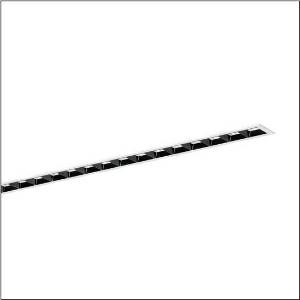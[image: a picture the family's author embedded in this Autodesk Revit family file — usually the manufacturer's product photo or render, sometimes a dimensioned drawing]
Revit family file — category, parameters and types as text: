
# Revit family: silica_r__21_51mx12dc4awb_60db
name_source: partatom
category: Lighting Fixtures
units: mm (PartAtom-declared; Revit-internal decimal feet)

## family parameters
Cut with Voids When Loaded = No
Host = Face
Light Source = No
Part Type = Normal
Room Calculation Point = No
Round Connector Dimension = Use Diameter
Shared = No

## types (1)
- --- (1 x LED, 10800 lm, 64.7 W, 4000K)
    Apparent Load = 65 VA
    CIE Flux Codes = 86 100 100 100 100
    Color Rendering = 80
    Color Temperature = 4000K
    Default Elevation = 1800 mm
    Description = Silica® 21, office luminaire, primary light control with darklight reflector, of PMMA, black, CAT 2 (L<= 3000cd/m²), light emission: direct distribution, primary light characteristic: symmetric, installation type: recessed, LED, rated luminous flux: 10.800lm, luminous efficacy: 167lm/W, light colour: 840, colour temperature: 4000K, with terminal, 3+2-pole, max. 2.5mm², mains connection: 220..240V, AC, 50/60Hz, rated input power: 64.7W, luminaire housing, of aluminium, traffic white (RAL 9016), length: 3.028mm, width: 79mm, height: 53mm, protection rating (complete): IP20, insulation class (complete): insulation class I (protective earthing), certification: CE, permissible operating ambient temperature: 0..+35°C, standard: EN 50419, packaging unit: 1 piece
    Height = 0 mm  [stored 0 ft]
    Lamp = 1 x LED
    Lamp Light Flux = 10800 lm
    Lamp Power = 64.7 W
    Lamp count = 1
    Length = 3027 mm
    Luminous efficacy = 167 lm/W
    Manufacturer = Siteco
    ModVariant = No
    Model = 51MX12DC4AWB
    Mounting Place = Ceiling
    Mounting Type = Recessed
    Number of Poles = 1
    OnlyDefault = Yes
    Power Factor = 1
    Product Name = Silica® 21
    Product group = office luminaire | ceiling recessed
    ProductGroupID = 400
    Protection Class = Protection class I
    Protection Degree = IP 20
    RLX_Detail_Level = 1
    RlxData = <blob elided: 62773 chars, md5=38e0fbbe>
    Socket = socket
    Standby Power = 0 W
    System Light Flux = 10800 lm
    System Power = 65 W
    Type Comments = factory setting: luminous flux: 100 % | dim-lin: 254 | 366 mA
    Type Image = l_1251632.jpg
    URL = http://relux.com
    VarID = @adj_034067
    Voltage = 0 V
    Weight = 0.00 kg
    Width = 79 mm

note: [stored X ft] marks values corroborated as IEEE doubles in the binary element streams (Revit-internal decimal feet)

## geometry (parser evidence)
native form markers: Blend x4, Sweep x11
no freeform markers — native parametric forms only
